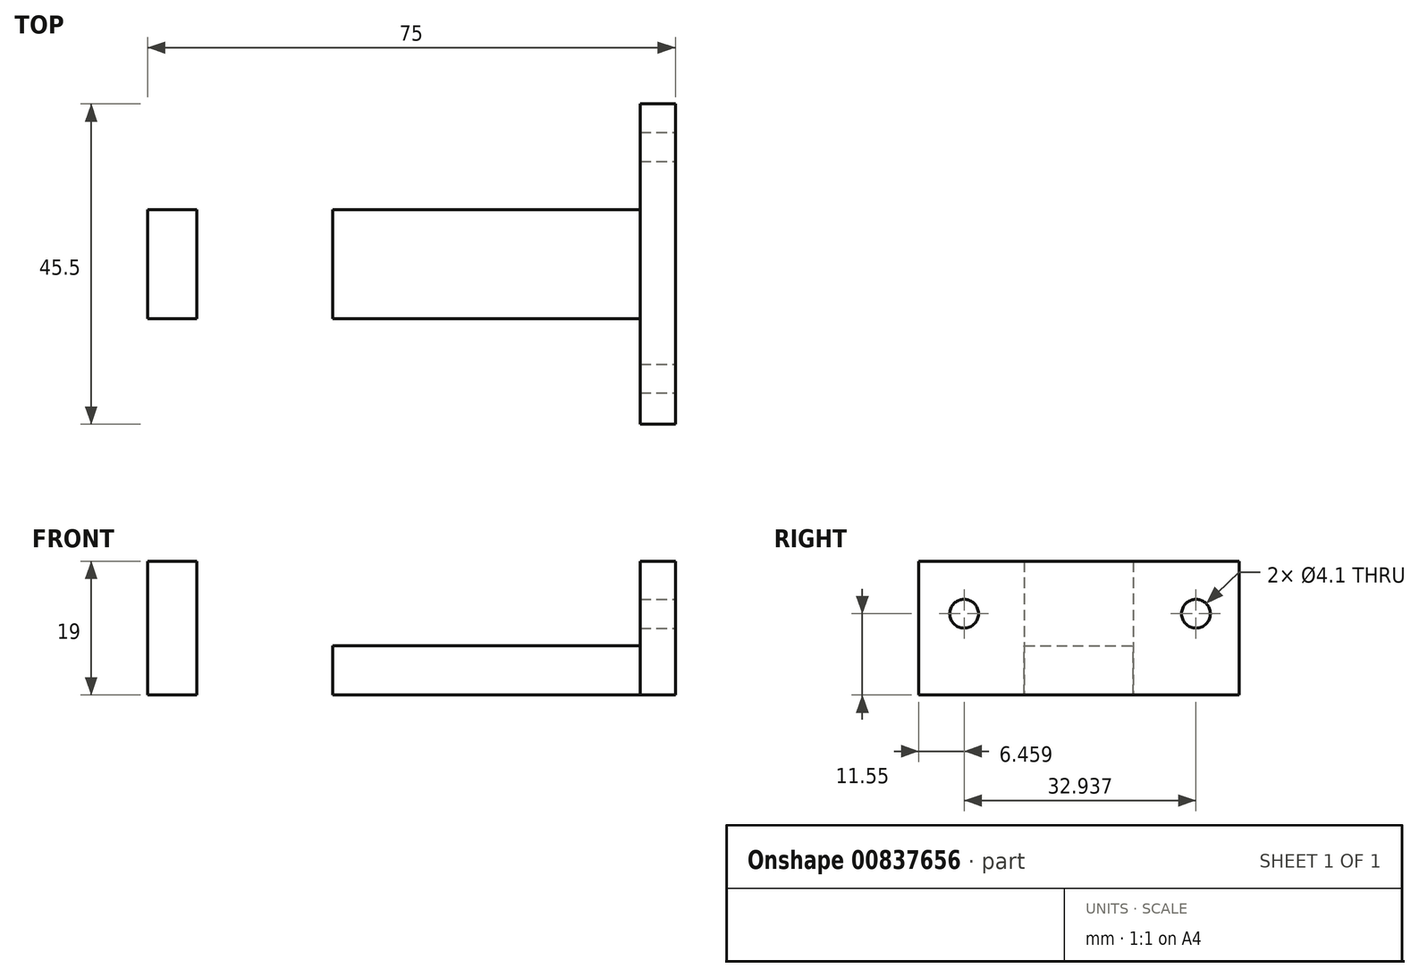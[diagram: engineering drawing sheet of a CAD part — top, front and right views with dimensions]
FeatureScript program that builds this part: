
annotation { "Feature Type Name" : "Feature", "Feature Type Description" : "" }
export const myFeature = defineFeature(function(context is Context, id is Id, definition is map)
    precondition{}
    {
        {
            var Q0;
            Q0=qCreatedBy(makeId("Top.planeOp"),FACE);
            var sketch = newSketch(context, id + "F0", { "sketchPlane" : qUnion([Q0])});
            skLineSegment(sketch, "E0.bottom", {"start": v(-23.33, -7.75) * mm, "end": v(-91.33, -7.75) * mm});
            skLineSegment(sketch, "E0.top", {"start": v(-23.33, 7.75) * mm, "end": v(-91.33, 7.75) * mm});
            skLineSegment(sketch, "E0.left", {"start": v(-23.33, -7.75) * mm, "end": v(-23.33, 7.75) * mm});
            skLineSegment(sketch, "E0.right", {"start": v(-91.33, -7.75) * mm, "end": v(-91.33, 7.75) * mm});
            skPoint(sketch, "E0.middle", {"position": v(-57.33, 0) * mm});
            skLineSegment(sketch, "E1.bottom", {"start": v(-98.33, 7.75) * mm, "end": v(-91.33, 7.75) * mm});
            skLineSegment(sketch, "E1.top", {"start": v(-98.33, -7.75) * mm, "end": v(-91.33, -7.75) * mm});
            skLineSegment(sketch, "E1.left", {"start": v(-91.33, 7.75) * mm, "end": v(-91.33, -7.75) * mm});
            skLineSegment(sketch, "E1.right", {"start": v(-98.33, 7.75) * mm, "end": v(-98.33, -7.75) * mm});
            skLineSegment(sketch, "E2.bottom", {"start": v(-78.99, 7.75) * mm, "end": v(-71.99, 7.75) * mm});
            skLineSegment(sketch, "E2.top", {"start": v(-78.99, -7.75) * mm, "end": v(-71.99, -7.75) * mm});
            skLineSegment(sketch, "E2.left", {"start": v(-78.99, 7.75) * mm, "end": v(-78.99, -7.75) * mm});
            skLineSegment(sketch, "E2.right", {"start": v(-71.99, 7.75) * mm, "end": v(-71.99, -7.75) * mm});
            skLineSegment(sketch, "E3", {"start": v(-28.33, 7.75) * mm, "end": v(-28.33, -7.75) * mm});
            skLineSegment(sketch, "E4.bottom", {"start": v(-28.33, 22.75) * mm, "end": v(-23.33, 22.75) * mm});
            skLineSegment(sketch, "E4.top", {"start": v(-28.33, -22.75) * mm, "end": v(-23.33, -22.75) * mm});
            skLineSegment(sketch, "E4.left", {"start": v(-28.33, 22.75) * mm, "end": v(-28.33, -22.75) * mm});
            skLineSegment(sketch, "E4.right", {"start": v(-23.33, 22.75) * mm, "end": v(-23.33, -22.75) * mm});
            skSolve(sketch);
        }
        {
            var Q0;
            Q0=makeQuery(id+"F0.imprint","IMPRINT",FACE,{"disambiguationData":[TD([[makeQuery(id+"F0.imprint","IMPRINT",EDGE,{"derivedFrom":sQuery(id+"F0.wireOp",EDGE,"E1.bottom")}),-1.0]])]});
            var Q1;
            {var subQ0=sQuery(id+"F0.wireOp",EDGE,"E1.left");Q1=makeQuery(id+"F0.imprint","IMPRINT",FACE,{"disambiguationData":[TD([[makeQuery(id+"F0.imprint","IMPRINT",EDGE,{"derivedFrom":subQ0}),1.0]])]});}
            var Q2;
            Q2=makeQuery(id+"F0.imprint","IMPRINT",FACE,{"disambiguationData":[TD([[makeQuery(id+"F0.imprint","IMPRINT",EDGE,{"derivedFrom":sQuery(id+"F0.wireOp",EDGE,"E2.bottom")}),-1.0]])]});
            var Q3;
            {var subQ0=sQuery(id+"F0.wireOp",EDGE,"E2.right");Q3=makeQuery(id+"F0.imprint","IMPRINT",FACE,{"disambiguationData":[TD([[makeQuery(id+"F0.imprint","IMPRINT",EDGE,{"derivedFrom":subQ0}),1.0]])]});}
            var Q4;
            {var subQ0=sQuery(id+"F0.wireOp",EDGE,"E0.left");Q4=makeQuery(id+"F0.imprint","IMPRINT",FACE,{"disambiguationData":[TD([[makeQuery(id+"F0.imprint","IMPRINT",EDGE,{"derivedFrom":subQ0}),1.0]])]});}
            extrude(context, id + "F1", {"entities" : qUnion([Q0, Q1, Q2, Q3, Q4]), "depth" : 7 * mm, "offsetDistance" : 25 * mm});
        }
        {
            var Q0;
            Q0=makeQuery(id+"F0.imprint","IMPRINT",FACE,{"disambiguationData":[TD([[makeQuery(id+"F0.imprint","IMPRINT",EDGE,{"derivedFrom":sQuery(id+"F0.wireOp",EDGE,"E1.bottom")}),-1.0]])]});
            var Q1;
            Q1=makeQuery(id+"F0.imprint","IMPRINT",FACE,{"disambiguationData":[TD([[makeQuery(id+"F0.imprint","IMPRINT",EDGE,{"derivedFrom":sQuery(id+"F0.wireOp",EDGE,"E2.bottom")}),-1.0]])]});
            var Q2;
            {var subQ0=sQuery(id+"F0.wireOp",EDGE,"E0.left");Q2=makeQuery(id+"F0.imprint","IMPRINT",FACE,{"disambiguationData":[TD([[makeQuery(id+"F0.imprint","IMPRINT",EDGE,{"derivedFrom":subQ0}),1.0]])]});}
            var Q3;
            {var subQ5=sQuery(id+"F0.wireOp",EDGE,"E4.bottom");Q3=makeQuery(id+"F0.imprint","IMPRINT",FACE,{"disambiguationData":[TD([[makeQuery(id+"F0.imprint","IMPRINT",EDGE,{"derivedFrom":subQ5}),-1.0]])]});}
            var Q4;
            {var subQ0=sQuery(id+"F0.wireOp",EDGE,"E4.right");var subQ1=sQuery(id+"F0.wireOp",EDGE,"E0.bottom");var subQ2=makeQuery(id+"F0.imprint","INTERSECT",VERTEX,{"derivedFrom":[subQ1,subQ0]});Q4=makeQuery(id+"F0.imprint","IMPRINT",FACE,{"disambiguationData":[TD([[makeQuery(id+"F0.imprint","IMPRINT",EDGE,{"disambiguationData":[TD([[subQ2,-1.0]])],"derivedFrom":subQ1}),-1.0]])]});}
            var Q5;
            {var subQ5=sQuery(id+"F0.wireOp",EDGE,"E4.top");Q5=makeQuery(id+"F0.imprint","IMPRINT",FACE,{"disambiguationData":[TD([[makeQuery(id+"F0.imprint","IMPRINT",EDGE,{"derivedFrom":subQ5}),1.0]])]});}
            extrude(context, id + "F2", {"entities" : qUnion([Q0, Q1, Q2, Q3, Q4, Q5]), "operationType" : NewBodyOperationType.ADD, "depth" : 19 * mm, "offsetDistance" : 25 * mm});
        }
        {
            var Q0;
            Q0=makeQuery(id+"F2.opExtrude","SWEPT_FACE",FACE,{"disambiguationData":[OSD([sQuery(id+"F0.wireOp",EDGE,"E4.right")])]});
            var sketch = newSketch(context, id + "F3", { "sketchPlane" : qUnion([Q0])});
            skLineSegment(sketch, "E5", {"start": v(-22.75, 9.5) * mm, "end": v(22.75, 9.5) * mm});
            skLineSegment(sketch, "E6", {"start": v(0, 19) * mm, "end": v(0, 0) * mm});
            skPoint(sketch, "E7", {"position": v(-11.37, 19) * mm});
            skPoint(sketch, "E8", {"position": v(-11.37, 0) * mm});
            skLineSegment(sketch, "E9", {"start": v(-11.37, 19) * mm, "end": v(-11.37, 0) * mm});
            skLineSegment(sketch, "E10", {"start": v(11.38, 19) * mm, "end": v(11.38, 0) * mm});
            skLineSegment(sketch, "E11", {"start": v(-22.75, 11.55) * mm, "end": v(22.75, 11.55) * mm});
            skCircle(sketch, "E12", {"center": v(-16.3, 11.55) * mm, "radius": 2.05 * mm});
            skCircle(sketch, "E13", {"center": v(16.65, 11.55) * mm, "radius": 2.05 * mm});
            skSolve(sketch);
        }
        {
            var Q0;
            {var subQ0=sQuery(id+"F3.wireOp",EDGE,"E12");var subQ1=sQuery(id+"F3.wireOp",EDGE,"E11");var subQ2=makeQuery(id+"F3.imprint","INTERSECT",VERTEX,{"disambiguationData":[OD(0.0)],"derivedFrom":[subQ1,subQ0]});Q0=makeQuery(id+"F3.imprint","IMPRINT",FACE,{"disambiguationData":[TD([[makeQuery(id+"F3.imprint","IMPRINT",EDGE,{"disambiguationData":[TD([[subQ2,-1.0]])],"derivedFrom":subQ1}),1.0]])]});}
            var Q1;
            {var subQ0=sQuery(id+"F3.wireOp",EDGE,"E12");var subQ1=sQuery(id+"F3.wireOp",EDGE,"E11");var subQ2=makeQuery(id+"F3.imprint","INTERSECT",VERTEX,{"disambiguationData":[OD(0.0)],"derivedFrom":[subQ1,subQ0]});Q1=makeQuery(id+"F3.imprint","IMPRINT",FACE,{"disambiguationData":[TD([[makeQuery(id+"F3.imprint","IMPRINT",EDGE,{"disambiguationData":[TD([[subQ2,-1.0]])],"derivedFrom":subQ1}),-1.0]])]});}
            var Q2;
            {var subQ0=sQuery(id+"F3.wireOp",EDGE,"E13");var subQ1=sQuery(id+"F3.wireOp",EDGE,"E11");var subQ2=makeQuery(id+"F3.imprint","INTERSECT",VERTEX,{"disambiguationData":[OD(0.0)],"derivedFrom":[subQ1,subQ0]});Q2=makeQuery(id+"F3.imprint","IMPRINT",FACE,{"disambiguationData":[TD([[makeQuery(id+"F3.imprint","IMPRINT",EDGE,{"disambiguationData":[TD([[subQ2,-1.0]])],"derivedFrom":subQ1}),1.0]])]});}
            var Q3;
            {var subQ0=sQuery(id+"F3.wireOp",EDGE,"E13");var subQ1=sQuery(id+"F3.wireOp",EDGE,"E11");var subQ2=makeQuery(id+"F3.imprint","INTERSECT",VERTEX,{"disambiguationData":[OD(0.0)],"derivedFrom":[subQ1,subQ0]});Q3=makeQuery(id+"F3.imprint","IMPRINT",FACE,{"disambiguationData":[TD([[makeQuery(id+"F3.imprint","IMPRINT",EDGE,{"disambiguationData":[TD([[subQ2,-1.0]])],"derivedFrom":subQ1}),-1.0]])]});}
            extrude(context, id + "F4", {"entities" : qUnion([Q0, Q1, Q2, Q3]), "operationType" : NewBodyOperationType.REMOVE, "oppositeDirection" : true, "depth" : 15 * mm, "offsetDistance" : 25 * mm});
        }
    });
